# Revit family: Electronics_Commercial-Loudspeakers_Biamp_Ceiling-Speaker_EN-CM5T6
name_source: partatom
category: Communication Devices
units: mm (PartAtom-declared; Revit-internal decimal feet)

## family parameters
Cut with Voids When Loaded = No
Host = Face
Maintain Annotation Orientation = No
OmniClass Number = 23.85.10.11.14.14.14
OmniClass Title = Loudspeakers
Part Type = Normal
Room Calculation Point = No
Round Connector Dimension = Use Diameter
Shared = No

## types (1)
- EN-CM5T6
    100V transformer power taps in watts = 6 - 3 - 1.5
    Ceiling thickness range in mm = 1 - 60
    Certificate ref = 1438/CPR/0351
    Closest RAL colour (subject to deviations) = RAL9010
    Colour = White
    Connector Description = Terminal strip; 100V operation
    Default Elevation = 48 "
    Depth = 6 "
    Description = EN-CM5T6 EN54-24 Certified 5 Ceiling Speaker
    Diameter = 7 "
    Frequency response in Hz = 320 - 19 k
    Grill Material = Biamp - Plastic - White(Grid)
    Housing Material = Biamp - Plastic - White
    IP rating = 50
    Loudspeaker system = Full range
    Low impedance dynamic power watts = 6
    Main construction material = Steel
    Manufacturer = Biamp
    Max SPL 1m in dB = 101,3
    Model = EN-CM5T6
    Mounting system = 3 clamps
    Operating temperatures = -20°C to +80°C
    Product Documentation Link = https://downloads.biamp.com
    Product Page URL = https://www.biamp.com
    Product data url = https://bimobject.com
    SPL 1W/1m in dB = 93,5
    URL = https://www.biamp.com
    Version = 1
    Vertical dispersion angle 1000 Hz = 180°
    Weight = 1.27 lb
    Woofer cone material = Coated paper
    Woofer size in inch = 5.25

## geometry (parser evidence)
native form markers: Sweep x2
no freeform markers — native parametric forms only
